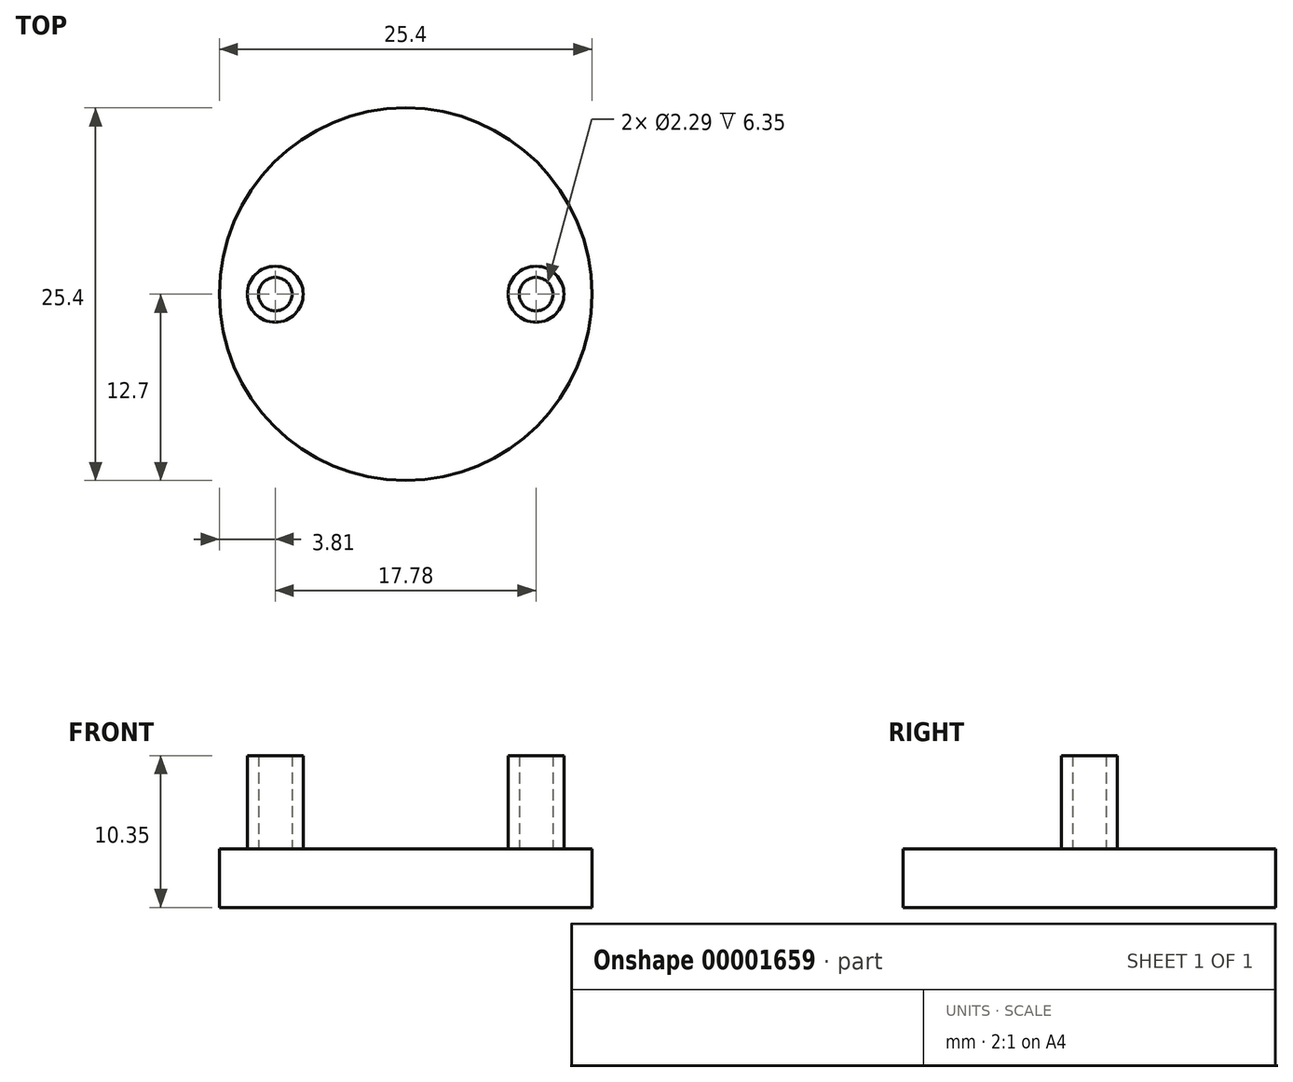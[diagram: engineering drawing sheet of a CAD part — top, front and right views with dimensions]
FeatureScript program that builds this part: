
annotation { "Feature Type Name" : "Feature", "Feature Type Description" : "" }
export const myFeature = defineFeature(function(context is Context, id is Id, definition is map)
    precondition{}
    {
        {
            var Q0;
            Q0=qCreatedBy(makeId("Top.planeOp"),FACE);
            var sketch = newSketch(context, id + "F0", { "sketchPlane" : qUnion([Q0])});
            skCircle(sketch, "E0", {"center": v(0, 0) * mm, "radius": 12.7 * mm});
            skSolve(sketch);
        }
        {
            var Q0;
            Q0=makeQuery(id+"F0.imprint","IMPRINT",FACE,{"disambiguationData":[TD([[makeQuery(id+"F0.imprint","IMPRINT",EDGE,{"derivedFrom":sQuery(id+"F0.wireOp",EDGE,"E0")}),1.0]])]});
            var Q1;
            {var subQ0=sQuery(id+"F0.wireOp",EDGE,"e25ec945-0176-42a3-8cc6-104fd248c407");Q1=makeQuery(id+"F0.imprint","IMPRINT",FACE,{"disambiguationData":[TD([[makeQuery(id+"F0.imprint","IMPRINT",EDGE,{"derivedFrom":subQ0}),1.0]])]});}
            var Q2;
            {var subQ1=sQuery(id+"F0.wireOp",EDGE,"c380ad6a-1380-49ba-a21a-42ae37bb6cb2");Q2=makeQuery(id+"F0.imprint","IMPRINT",FACE,{"disambiguationData":[TD([[makeQuery(id+"F0.imprint","IMPRINT",EDGE,{"derivedFrom":subQ1}),-1.0]])]});}
            var Q3;
            {var subQ1=sQuery(id+"F0.wireOp",EDGE,"ff710814-4745-44aa-b676-e5d5ac8fc730");Q3=makeQuery(id+"F0.imprint","IMPRINT",FACE,{"disambiguationData":[TD([[makeQuery(id+"F0.imprint","IMPRINT",EDGE,{"derivedFrom":subQ1}),1.0]])]});}
            var Q4;
            {var subQ0=sQuery(id+"F0.wireOp",EDGE,"e7685be8-6828-4ce3-8f4e-fd06af8c092b");Q4=makeQuery(id+"F0.imprint","IMPRINT",FACE,{"disambiguationData":[TD([[makeQuery(id+"F0.imprint","IMPRINT",EDGE,{"derivedFrom":subQ0}),-1.0]])]});}
            extrude(context, id + "F1", {"entities" : qUnion([Q0, Q1, Q2, Q3, Q4]), "depth" : 4 * mm});
        }
        {
            var Q0;
            Q0=makeQuery(id+"F1.opExtrude","CAP_FACE",FACE,{"disambiguationData":[OSD([sQuery(id+"F0.wireOp",EDGE,"E0"),sQuery(id+"F0.wireOp",EDGE,"ee2b142d-7153-4939-b7e2-92997c54bb4b"),sQuery(id+"F0.wireOp",EDGE,"e25ec945-0176-42a3-8cc6-104fd248c407"),sQuery(id+"F0.wireOp",EDGE,"e7685be8-6828-4ce3-8f4e-fd06af8c092b"),sQuery(id+"F0.wireOp",EDGE,"c380ad6a-1380-49ba-a21a-42ae37bb6cb2"),sQuery(id+"F0.wireOp",EDGE,"ff710814-4745-44aa-b676-e5d5ac8fc730"),sQuery(id+"F0.wireOp",EDGE,"6b73cb07-faf3-4202-9543-59a286bdfcf8"),sQuery(id+"F0.wireOp",EDGE,"7c5b0f06-869f-4826-862d-39f97500ed2d")])],"isStart":false});
            var sketch = newSketch(context, id + "F2", { "sketchPlane" : qUnion([Q0])});
            skCircle(sketch, "E1", {"center": v(-8.9, 0) * mm, "radius": 1.9 * mm});
            skCircle(sketch, "E2", {"center": v(8.9, 0) * mm, "radius": 1.9 * mm});
            skCircle(sketch, "E3", {"center": v(-8.9, 0) * mm, "radius": 1.14 * mm});
            skCircle(sketch, "E4", {"center": v(8.9, 0) * mm, "radius": 1.14 * mm});
            skSolve(sketch);
        }
        {
            var Q0;
            Q0=makeQuery(id+"F2.imprint","IMPRINT",FACE,{"disambiguationData":[TD([[makeQuery(id+"F2.imprint","IMPRINT",EDGE,{"derivedFrom":sQuery(id+"F2.wireOp",EDGE,"E1")}),1.0]])]});
            var Q1;
            Q1=makeQuery(id+"F2.imprint","IMPRINT",FACE,{"disambiguationData":[TD([[makeQuery(id+"F2.imprint","IMPRINT",EDGE,{"derivedFrom":sQuery(id+"F2.wireOp",EDGE,"E2")}),1.0]])]});
            extrude(context, id + "F3", {"entities" : qUnion([Q0, Q1]), "operationType" : NewBodyOperationType.ADD, "depth" : 6.35 * mm});
        }
    });
